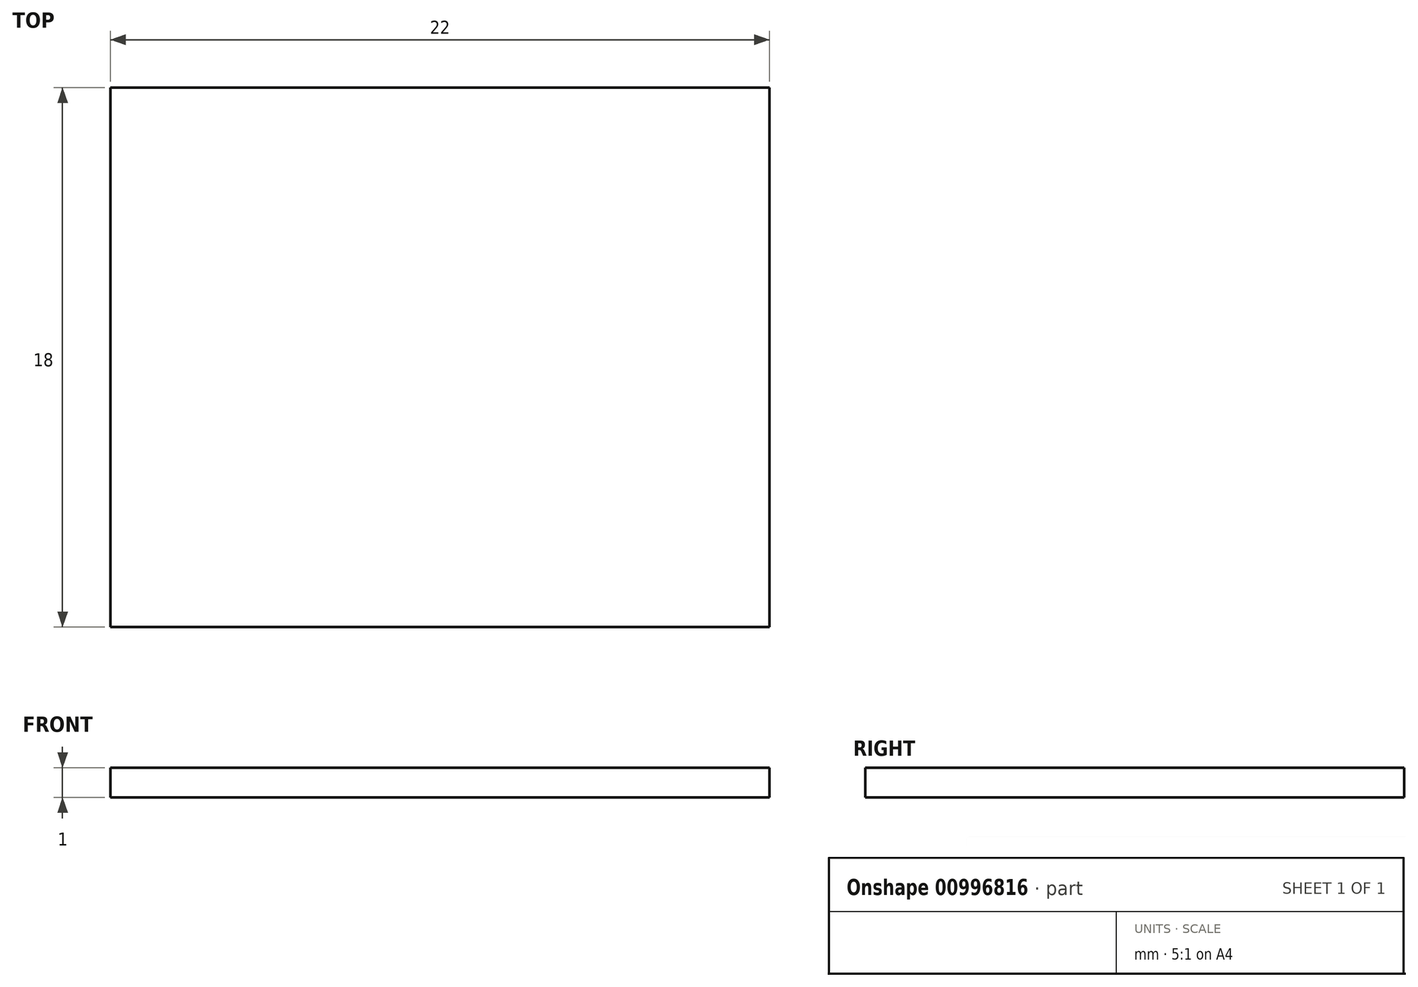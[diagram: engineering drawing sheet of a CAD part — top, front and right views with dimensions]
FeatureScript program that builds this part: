
annotation { "Feature Type Name" : "Feature", "Feature Type Description" : "" }
export const myFeature = defineFeature(function(context is Context, id is Id, definition is map)
    precondition{}
    {
        {
            var Q0;
            Q0=qCreatedBy(makeId("Top.planeOp"),FACE);
            var sketch = newSketch(context, id + "F0", { "sketchPlane" : qUnion([Q0])});
            skLineSegment(sketch, "E0.bottom", {"start": v(11, 9) * mm, "end": v(-11, 9) * mm});
            skLineSegment(sketch, "E0.top", {"start": v(11, -9) * mm, "end": v(-11, -9) * mm});
            skLineSegment(sketch, "E0.left", {"start": v(11, 9) * mm, "end": v(11, -9) * mm});
            skLineSegment(sketch, "E0.right", {"start": v(-11, 9) * mm, "end": v(-11, -9) * mm});
            skPoint(sketch, "E0.middle", {"position": v(0, 0) * mm});
            skSolve(sketch);
        }
        {
            var Q0;
            Q0=makeQuery(id+"F0.imprint","IMPRINT",FACE,{"disambiguationData":[TD([[makeQuery(id+"F0.imprint","IMPRINT",EDGE,{"derivedFrom":sQuery(id+"F0.wireOp",EDGE,"E0.bottom")}),1.0]])]});
            extrude(context, id + "F1", {"entities" : qUnion([Q0]), "depth" : 1 * mm, "offsetDistance" : 25 * mm});
        }
    });
